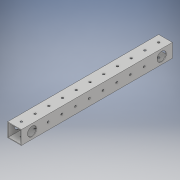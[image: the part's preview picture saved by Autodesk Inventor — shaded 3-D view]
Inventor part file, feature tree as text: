
AUTODESK INVENTOR PART (.ipt)
format: ipt  version: 2018 (Build 220112000, 112)  size: 174,592 bytes
history: native  units: in
note: dims shown in document units (in); Inventor stores cm internally (conversion verified against a paired STEP export)
features: extrude x4, sketch x4, shell x1
ambient origin geometry x8: Origin, YZ Plane, XZ Plane, XY Plane, X Axis, Y Axis, Z Axis, Center Point
bodies: Solid1 (feature_tree)
feature tree (9):
  extrude  "Extrusion1"  Depth=1.0in
  shell  "Shell1"  Thickness=11.0in
  extrude  "Extrusion2"  Depth=0.045in
  extrude  "Extrusion3"  Depth=0.5in
  extrude  "Extrusion4"  Depth=11.0in
  sketch  "Sketch1"  dims[d0=1.0in d1=1.0in d2=11.0in d3=0.0in]
  sketch  "Sketch2"  dims[d4=0.045in d5=0.675in]
  sketch  "Sketch3"  dims[d6=0.7815in d7=0.5in]
  sketch  "Sketch4"  dims[d8=0.675in d9=0.7815in d10=0.5in d11=11.0in d12=0.0in d13=0.15in d14=0.5in d15=0.5in d16=4.3307in d18=1.0in d19=0.3937in d21=1.0in d23=11.0in d24=0.0in d25=0.15in d26=0.5in d27=0.1625in d28=3.5433in d30=1.0in d31=0.3937in d33=1.0in d35=11.0in d36=0.0in]
